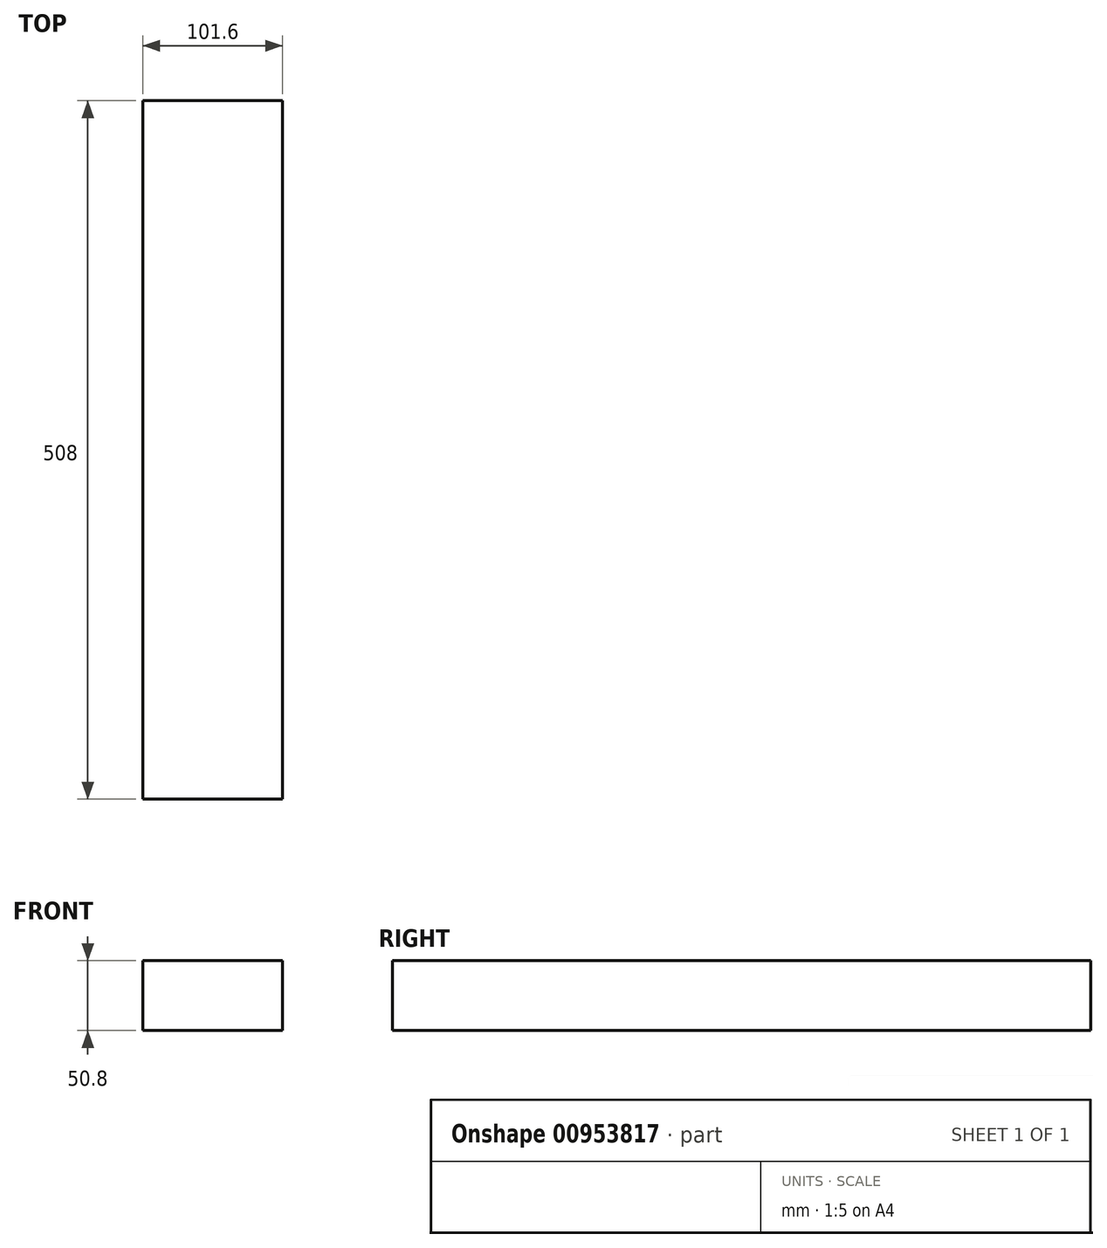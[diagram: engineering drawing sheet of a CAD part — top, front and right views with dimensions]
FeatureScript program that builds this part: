
annotation { "Feature Type Name" : "Feature", "Feature Type Description" : "" }
export const myFeature = defineFeature(function(context is Context, id is Id, definition is map)
    precondition{}
    {
        {
            var Q0;
            Q0=qCreatedBy(makeId("Front.planeOp"),FACE);
            var sketch = newSketch(context, id + "F0", { "sketchPlane" : qUnion([Q0])});
            skLineSegment(sketch, "E0.bottom", {"start": v(-50.8, -25.4) * mm, "end": v(50.8, -25.4) * mm});
            skLineSegment(sketch, "E0.top", {"start": v(-50.8, 25.4) * mm, "end": v(50.8, 25.4) * mm});
            skLineSegment(sketch, "E0.left", {"start": v(-50.8, -25.4) * mm, "end": v(-50.8, 25.4) * mm});
            skLineSegment(sketch, "E0.right", {"start": v(50.8, -25.4) * mm, "end": v(50.8, 25.4) * mm});
            skPoint(sketch, "E0.middle", {"position": v(0, 0) * mm});
            skSolve(sketch);
        }
        {
            var Q0;
            Q0 = qSketchRegion(id + "F0", true);
            extrude(context, id + "F1", {"entities" : qUnion([Q0]), "depth" : 508 * mm, "offsetDistance" : 25.4 * mm});
        }
    });
